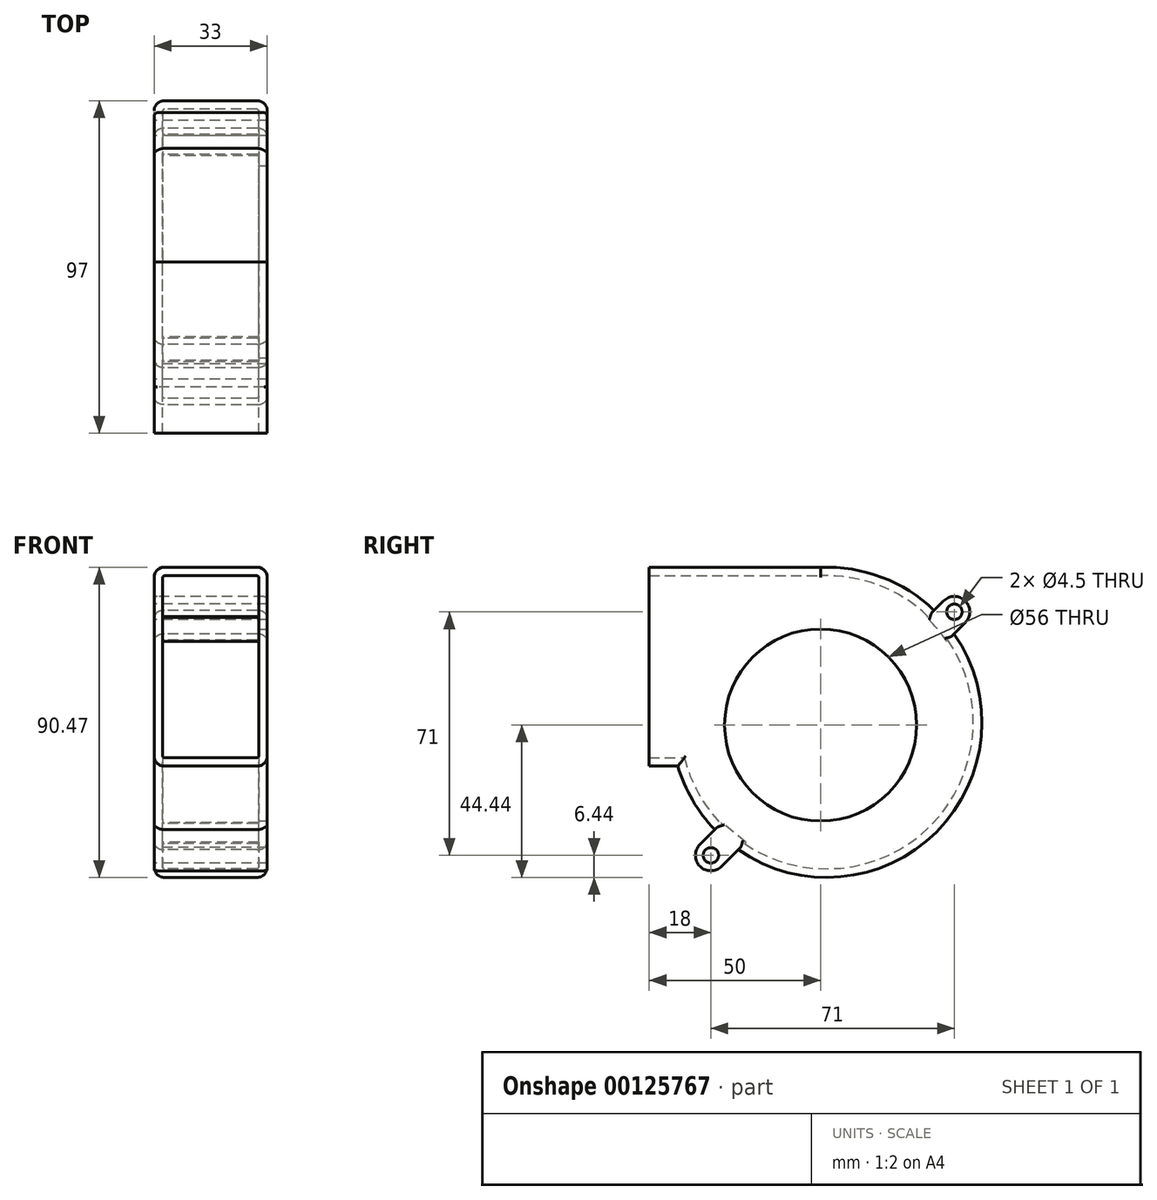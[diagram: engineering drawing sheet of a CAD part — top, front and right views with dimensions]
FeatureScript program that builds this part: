
annotation { "Feature Type Name" : "Feature", "Feature Type Description" : "" }
export const myFeature = defineFeature(function(context is Context, id is Id, definition is map)
    precondition{}
    {
        {
            var Q0;
            Q0=qCreatedBy(makeId("Right.planeOp"),FACE);
            var sketch = newSketch(context, id + "F0", { "sketchPlane" : qUnion([Q0])});
            skLineSegment(sketch, "E0", {"start": v(0, 53.62) * mm, "end": v(0, -54.86) * mm, "construction": true});
            skLineSegment(sketch, "E1", {"start": v(-55.86, 0) * mm, "end": v(54.86, 0) * mm, "construction": true});
            skLineSegment(sketch, "E2", {"start": v(0, 52) * mm, "end": v(-50, 52) * mm});
            skLineSegment(sketch, "E3", {"start": v(47, 45.16) * mm, "end": v(47, -48.4) * mm, "construction": true});
            skLineSegment(sketch, "E4", {"start": v(-57.85, -38.44) * mm, "end": v(57.85, -38.44) * mm, "construction": true});
            skLineSegment(sketch, "E5", {"start": v(-50, 52) * mm, "end": v(-50, -6) * mm});
            skLineSegment(sketch, "E6", {"start": v(-50, -6) * mm, "end": v(-41.63, -6) * mm});
            skPoint(sketch, "E7.2.internal.snap0", {"position": v(0, -38.44) * mm});
            skArc(sketch, "E8", {"start": v(-41.63, -6) * mm, "mid": v(38.51, -19.58) * mm, "end": v(0, 52) * mm});
            skPoint(sketch, "E8.second.point", {"position": v(-11.37, -36.5) * mm});
            skPoint(sketch, "E8.third.point", {"position": v(32.48, -26.41) * mm});
            skSolve(sketch);
        }
        {
            var Q0;
            Q0 = qSketchRegion(id + "F0", true);
            extrude(context, id + "F1", {"entities" : qUnion([Q0]), "endBound" : BoundingType.SYMMETRIC, "depth" : 33 * mm});
        }
        {
            var Q0;
            Q0=qCreatedBy(makeId("Right.planeOp"),FACE);
            var sketch = newSketch(context, id + "F2", { "sketchPlane" : qUnion([Q0])});
            skCircle(sketch, "E9", {"center": v(39, 39) * mm, "radius": 2.25 * mm});
            skCircle(sketch, "E10", {"center": v(-32, -32) * mm, "radius": 2.25 * mm});
            skLineSegment(sketch, "E11", {"start": v(39, 39) * mm, "end": v(0, 0) * mm, "construction": true});
            skLineSegment(sketch, "E12", {"start": v(0, 0) * mm, "end": v(-32, -32) * mm, "construction": true});
            skArc(sketch, "E13", {"start": v(42.18, 35.82) * mm, "mid": v(42.18, 42.18) * mm, "end": v(35.82, 42.18) * mm});
            skArc(sketch, "E14", {"start": v(-35.18, -28.82) * mm, "mid": v(-35.18, -35.18) * mm, "end": v(-28.82, -35.18) * mm});
            skLineSegment(sketch, "E15", {"start": v(35.82, 42.18) * mm, "end": v(30.96, 37.32) * mm});
            skLineSegment(sketch, "E16", {"start": v(42.18, 35.82) * mm, "end": v(36.78, 30.42) * mm});
            skLineSegment(sketch, "E17", {"start": v(-35.18, -28.82) * mm, "end": v(-28.76, -22.4) * mm});
            skLineSegment(sketch, "E18", {"start": v(-28.76, -22.4) * mm, "end": v(-21.86, -28.22) * mm});
            skLineSegment(sketch, "E19", {"start": v(-21.86, -28.22) * mm, "end": v(-28.82, -35.18) * mm});
            skArc(sketch, "E20", {"start": v(-28.76, -22.4) * mm, "mid": v(-25.47, -25.5) * mm, "end": v(-21.86, -28.22) * mm});
            skPoint(sketch, "E20.third.point", {"position": v(0.44, -35.42) * mm});
            skArc(sketch, "E21.trimOffspring", {"start": v(36.78, 30.42) * mm, "mid": v(34.05, 34.02) * mm, "end": v(30.96, 37.32) * mm});
            skSolve(sketch);
        }
        {
            var Q0;
            Q0=makeQuery(id+"F1.opExtrude","CAP_EDGE",EDGE,{"disambiguationData":[OSD([sQuery(id+"F0.wireOp",EDGE,"E2")])],"isStart":false});
            var Q1;
            Q1=makeQuery(id+"F1.opExtrude","CAP_EDGE",EDGE,{"disambiguationData":[OSD([sQuery(id+"F0.wireOp",EDGE,"E8")])],"isStart":false});
            var Q2;
            Q2=makeQuery(id+"F1.opExtrude","CAP_EDGE",EDGE,{"disambiguationData":[OSD([sQuery(id+"F0.wireOp",EDGE,"E6")])],"isStart":false});
            var Q3;
            Q3=makeQuery(id+"F1.opExtrude","CAP_EDGE",EDGE,{"disambiguationData":[OSD([sQuery(id+"F0.wireOp",EDGE,"E2")])],"isStart":true});
            var Q4;
            Q4=makeQuery(id+"F1.opExtrude","CAP_EDGE",EDGE,{"disambiguationData":[OSD([sQuery(id+"F0.wireOp",EDGE,"E8")])],"isStart":true});
            var Q5;
            Q5=makeQuery(id+"F1.opExtrude","CAP_EDGE",EDGE,{"disambiguationData":[OSD([sQuery(id+"F0.wireOp",EDGE,"E6")])],"isStart":true});
            fillet(context, id + "F3", {"entities" : qUnion([Q0, Q1, Q2, Q3, Q4, Q5]), "radius" : 3 * mm, "tangentPropagation" : true, "allowEdgeOverflow" : false});
        }
        {
            var Q0;
            Q0=makeQuery(id+"F1.opExtrude","SWEPT_FACE",FACE,{"disambiguationData":[OSD([sQuery(id+"F0.wireOp",EDGE,"E5")])]});
            shell(context, id + "F4", {"entities" : qUnion([Q0]), "thickness" : 2.5 * mm});
        }
        {
            var Q0;
            Q0 = qSketchRegion(id + "F2", true);
            extrude(context, id + "F5", {"entities" : qUnion([Q0]), "operationType" : NewBodyOperationType.ADD, "endBound" : BoundingType.SYMMETRIC, "depth" : 33 * mm});
        }
        {
            var Q0;
            Q0=makeQuery(id+"F5.opExtrude","CAP_EDGE",EDGE,{"disambiguationData":[OSD([sQuery(id+"F2.wireOp",EDGE,"E17")])],"isStart":false});
            var Q1;
            Q1=makeQuery(id+"F5.opExtrude","CAP_EDGE",EDGE,{"disambiguationData":[OSD([sQuery(id+"F2.wireOp",EDGE,"E14")])],"isStart":false});
            var Q2;
            Q2=makeQuery(id+"F5.opExtrude","CAP_EDGE",EDGE,{"disambiguationData":[OSD([sQuery(id+"F2.wireOp",EDGE,"E19")])],"isStart":false});
            var Q3;
            Q3=makeQuery(id+"F5.opExtrude","CAP_EDGE",EDGE,{"disambiguationData":[OSD([sQuery(id+"F2.wireOp",EDGE,"E15")])],"isStart":false});
            var Q4;
            Q4=makeQuery(id+"F5.opExtrude","CAP_EDGE",EDGE,{"disambiguationData":[OSD([sQuery(id+"F2.wireOp",EDGE,"E13")])],"isStart":false});
            var Q5;
            Q5=makeQuery(id+"F5.opExtrude","CAP_EDGE",EDGE,{"disambiguationData":[OSD([sQuery(id+"F2.wireOp",EDGE,"E16")])],"isStart":false});
            var Q6;
            Q6=makeQuery(id+"F5.opExtrude","CAP_EDGE",EDGE,{"disambiguationData":[OSD([sQuery(id+"F2.wireOp",EDGE,"E16")])],"isStart":true});
            var Q7;
            Q7=makeQuery(id+"F5.opExtrude","CAP_EDGE",EDGE,{"disambiguationData":[OSD([sQuery(id+"F2.wireOp",EDGE,"E13")])],"isStart":true});
            var Q8;
            Q8=makeQuery(id+"F5.opExtrude","CAP_EDGE",EDGE,{"disambiguationData":[OSD([sQuery(id+"F2.wireOp",EDGE,"E19")])],"isStart":true});
            var Q9;
            Q9=makeQuery(id+"F5.opExtrude","CAP_EDGE",EDGE,{"disambiguationData":[OSD([sQuery(id+"F2.wireOp",EDGE,"E14")])],"isStart":true});
            fillet(context, id + "F6", {"entities" : qUnion([Q0, Q1, Q2, Q3, Q4, Q5, Q6, Q7, Q8, Q9]), "radius" : 1 * mm, "tangentPropagation" : true, "allowEdgeOverflow" : false});
        }
        {
            var Q0;
            Q0=makeQuery(id+"F5.boolean.opBoolean","MERGE",FACE,{"derivedFrom":[makeQuery(id+"F1.opExtrude","CAP_FACE",FACE,{"disambiguationData":[OSD([sQuery(id+"F0.wireOp",EDGE,"E2"),sQuery(id+"F0.wireOp",EDGE,"E5"),sQuery(id+"F0.wireOp",EDGE,"E6"),sQuery(id+"F0.wireOp",EDGE,"E8")])],"isStart":false}),makeQuery(id+"F5.opExtrude","CAP_FACE",FACE,{"disambiguationData":[OSD([sQuery(id+"F2.wireOp",EDGE,"E9"),sQuery(id+"F2.wireOp",EDGE,"E13"),sQuery(id+"F2.wireOp",EDGE,"E15"),sQuery(id+"F2.wireOp",EDGE,"E16"),sQuery(id+"F2.wireOp",EDGE,"E21.trimOffspring")])],"isStart":false}),makeQuery(id+"F5.opExtrude","CAP_FACE",FACE,{"disambiguationData":[OSD([sQuery(id+"F2.wireOp",EDGE,"E10"),sQuery(id+"F2.wireOp",EDGE,"E14"),sQuery(id+"F2.wireOp",EDGE,"E17"),sQuery(id+"F2.wireOp",EDGE,"E18"),sQuery(id+"F2.wireOp",EDGE,"E19")])],"isStart":false})]});
            var sketch = newSketch(context, id + "F7", { "sketchPlane" : qUnion([Q0])});
            skCircle(sketch, "E22", {"center": v(0, 6) * mm, "radius": 28 * mm});
            skSolve(sketch);
        }
        {
            var Q0;
            Q0=makeQuery(id+"F7.imprint","IMPRINT",FACE,{"disambiguationData":[TD([[makeQuery(id+"F7.imprint","IMPRINT",EDGE,{"derivedFrom":sQuery(id+"F7.wireOp",EDGE,"E22")}),1.0]])]});
            extrude(context, id + "F8", {"entities" : qUnion([Q0]), "operationType" : NewBodyOperationType.REMOVE, "oppositeDirection" : true, "depth" : 5 * mm});
        }
    });
